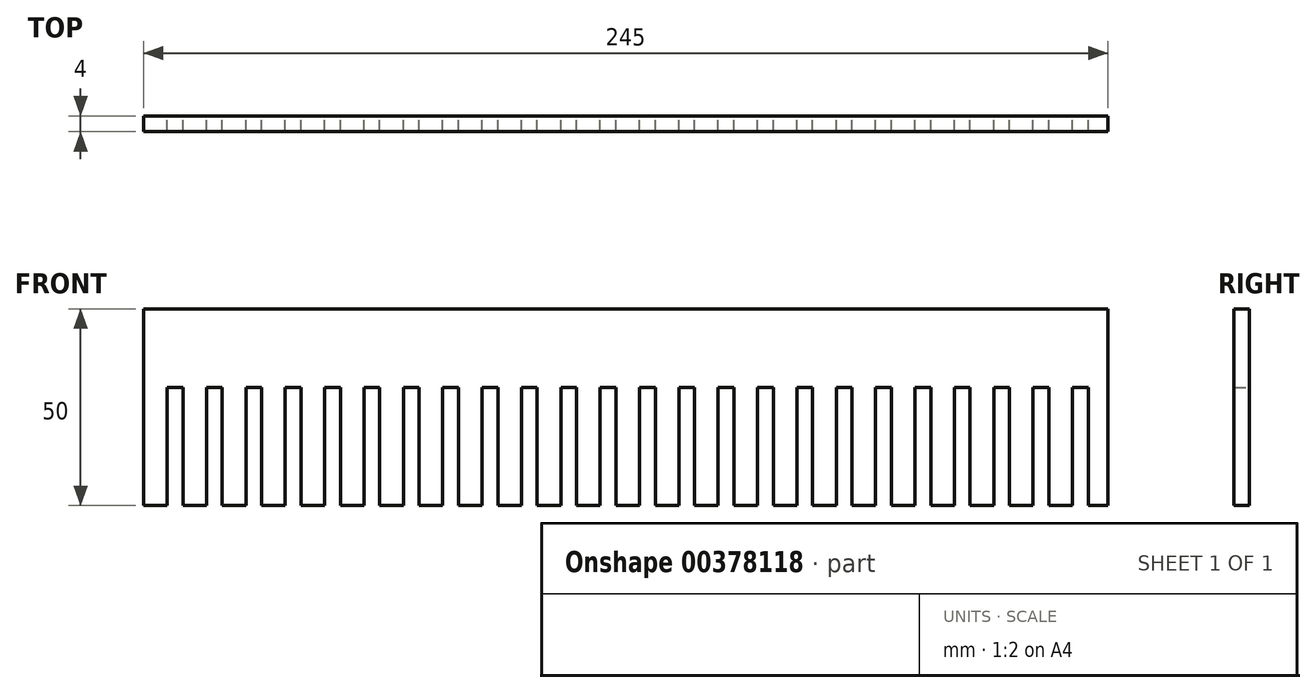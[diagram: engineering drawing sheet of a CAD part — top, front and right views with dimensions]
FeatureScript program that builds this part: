
annotation { "Feature Type Name" : "Feature", "Feature Type Description" : "" }
export const myFeature = defineFeature(function(context is Context, id is Id, definition is map)
    precondition{}
    {
        {
            var Q0;
            Q0=qCreatedBy(makeId("Front.planeOp"),FACE);
            var sketch = newSketch(context, id + "F0", { "sketchPlane" : qUnion([Q0])});
            skLineSegment(sketch, "E0", {"start": v(6, -20) * mm, "end": v(10, -20) * mm});
            skLineSegment(sketch, "E1", {"start": v(10, -20) * mm, "end": v(10, -50) * mm});
            skLineSegment(sketch, "E2.23.0.3", {"start": v(245, -50) * mm, "end": v(245, 0) * mm});
            skLineSegment(sketch, "E3", {"start": v(6, -20) * mm, "end": v(6, -50) * mm});
            skLineSegment(sketch, "E4", {"start": v(6, -50) * mm, "end": v(0, -50) * mm});
            skLineSegment(sketch, "E5", {"start": v(0, -50) * mm, "end": v(0, 0) * mm});
            skLineSegment(sketch, "E6", {"start": v(245, 0) * mm, "end": v(0, 0) * mm});
            skLineSegment(sketch, "E7.1.0.0", {"start": v(16, -50) * mm, "end": v(10, -50) * mm});
            skLineSegment(sketch, "E7.1.0.1", {"start": v(16, -20) * mm, "end": v(16, -50) * mm});
            skLineSegment(sketch, "E7.1.0.2", {"start": v(16, -20) * mm, "end": v(20, -20) * mm});
            skLineSegment(sketch, "E7.1.0.3", {"start": v(20, -20) * mm, "end": v(20, -50) * mm});
            skLineSegment(sketch, "E7.2.0.0", {"start": v(26, -50) * mm, "end": v(20, -50) * mm});
            skLineSegment(sketch, "E7.2.0.1", {"start": v(26, -20) * mm, "end": v(26, -50) * mm});
            skLineSegment(sketch, "E7.2.0.2", {"start": v(26, -20) * mm, "end": v(30, -20) * mm});
            skLineSegment(sketch, "E7.2.0.3", {"start": v(30, -20) * mm, "end": v(30, -50) * mm});
            skLineSegment(sketch, "E7.3.0.0", {"start": v(36, -50) * mm, "end": v(30, -50) * mm});
            skLineSegment(sketch, "E7.3.0.1", {"start": v(36, -20) * mm, "end": v(36, -50) * mm});
            skLineSegment(sketch, "E7.3.0.2", {"start": v(36, -20) * mm, "end": v(40, -20) * mm});
            skLineSegment(sketch, "E7.3.0.3", {"start": v(40, -20) * mm, "end": v(40, -50) * mm});
            skLineSegment(sketch, "E7.4.0.0", {"start": v(46, -50) * mm, "end": v(40, -50) * mm});
            skLineSegment(sketch, "E7.4.0.1", {"start": v(46, -20) * mm, "end": v(46, -50) * mm});
            skLineSegment(sketch, "E7.4.0.2", {"start": v(46, -20) * mm, "end": v(50, -20) * mm});
            skLineSegment(sketch, "E7.4.0.3", {"start": v(50, -20) * mm, "end": v(50, -50) * mm});
            skLineSegment(sketch, "E7.5.0.0", {"start": v(56, -50) * mm, "end": v(50, -50) * mm});
            skLineSegment(sketch, "E7.5.0.1", {"start": v(56, -20) * mm, "end": v(56, -50) * mm});
            skLineSegment(sketch, "E7.5.0.2", {"start": v(56, -20) * mm, "end": v(60, -20) * mm});
            skLineSegment(sketch, "E7.5.0.3", {"start": v(60, -20) * mm, "end": v(60, -50) * mm});
            skLineSegment(sketch, "E7.6.0.0", {"start": v(66, -50) * mm, "end": v(60, -50) * mm});
            skLineSegment(sketch, "E7.6.0.1", {"start": v(66, -20) * mm, "end": v(66, -50) * mm});
            skLineSegment(sketch, "E7.6.0.2", {"start": v(66, -20) * mm, "end": v(70, -20) * mm});
            skLineSegment(sketch, "E7.6.0.3", {"start": v(70, -20) * mm, "end": v(70, -50) * mm});
            skLineSegment(sketch, "E7.7.0.0", {"start": v(76, -50) * mm, "end": v(70, -50) * mm});
            skLineSegment(sketch, "E7.7.0.1", {"start": v(76, -20) * mm, "end": v(76, -50) * mm});
            skLineSegment(sketch, "E7.7.0.2", {"start": v(76, -20) * mm, "end": v(80, -20) * mm});
            skLineSegment(sketch, "E7.7.0.3", {"start": v(80, -20) * mm, "end": v(80, -50) * mm});
            skLineSegment(sketch, "E7.8.0.0", {"start": v(86, -50) * mm, "end": v(80, -50) * mm});
            skLineSegment(sketch, "E7.8.0.1", {"start": v(86, -20) * mm, "end": v(86, -50) * mm});
            skLineSegment(sketch, "E7.8.0.2", {"start": v(86, -20) * mm, "end": v(90, -20) * mm});
            skLineSegment(sketch, "E7.8.0.3", {"start": v(90, -20) * mm, "end": v(90, -50) * mm});
            skLineSegment(sketch, "E7.9.0.0", {"start": v(96, -50) * mm, "end": v(90, -50) * mm});
            skLineSegment(sketch, "E7.9.0.1", {"start": v(96, -20) * mm, "end": v(96, -50) * mm});
            skLineSegment(sketch, "E7.9.0.2", {"start": v(96, -20) * mm, "end": v(100, -20) * mm});
            skLineSegment(sketch, "E7.9.0.3", {"start": v(100, -20) * mm, "end": v(100, -50) * mm});
            skLineSegment(sketch, "E7.10.0.0", {"start": v(106, -50) * mm, "end": v(100, -50) * mm});
            skLineSegment(sketch, "E7.10.0.1", {"start": v(106, -20) * mm, "end": v(106, -50) * mm});
            skLineSegment(sketch, "E7.10.0.2", {"start": v(106, -20) * mm, "end": v(110, -20) * mm});
            skLineSegment(sketch, "E7.10.0.3", {"start": v(110, -20) * mm, "end": v(110, -50) * mm});
            skLineSegment(sketch, "E7.11.0.0", {"start": v(116, -50) * mm, "end": v(110, -50) * mm});
            skLineSegment(sketch, "E7.11.0.1", {"start": v(116, -20) * mm, "end": v(116, -50) * mm});
            skLineSegment(sketch, "E7.11.0.2", {"start": v(116, -20) * mm, "end": v(120, -20) * mm});
            skLineSegment(sketch, "E7.11.0.3", {"start": v(120, -20) * mm, "end": v(120, -50) * mm});
            skLineSegment(sketch, "E7.12.0.0", {"start": v(126, -50) * mm, "end": v(120, -50) * mm});
            skLineSegment(sketch, "E7.12.0.1", {"start": v(126, -20) * mm, "end": v(126, -50) * mm});
            skLineSegment(sketch, "E7.12.0.2", {"start": v(126, -20) * mm, "end": v(130, -20) * mm});
            skLineSegment(sketch, "E7.12.0.3", {"start": v(130, -20) * mm, "end": v(130, -50) * mm});
            skLineSegment(sketch, "E7.13.0.0", {"start": v(136, -50) * mm, "end": v(130, -50) * mm});
            skLineSegment(sketch, "E7.13.0.1", {"start": v(136, -20) * mm, "end": v(136, -50) * mm});
            skLineSegment(sketch, "E7.13.0.2", {"start": v(136, -20) * mm, "end": v(140, -20) * mm});
            skLineSegment(sketch, "E7.13.0.3", {"start": v(140, -20) * mm, "end": v(140, -50) * mm});
            skLineSegment(sketch, "E7.14.0.0", {"start": v(146, -50) * mm, "end": v(140, -50) * mm});
            skLineSegment(sketch, "E7.14.0.1", {"start": v(146, -20) * mm, "end": v(146, -50) * mm});
            skLineSegment(sketch, "E7.14.0.2", {"start": v(146, -20) * mm, "end": v(150, -20) * mm});
            skLineSegment(sketch, "E7.14.0.3", {"start": v(150, -20) * mm, "end": v(150, -50) * mm});
            skLineSegment(sketch, "E7.15.0.0", {"start": v(156, -50) * mm, "end": v(150, -50) * mm});
            skLineSegment(sketch, "E7.15.0.1", {"start": v(156, -20) * mm, "end": v(156, -50) * mm});
            skLineSegment(sketch, "E7.15.0.2", {"start": v(156, -20) * mm, "end": v(160, -20) * mm});
            skLineSegment(sketch, "E7.15.0.3", {"start": v(160, -20) * mm, "end": v(160, -50) * mm});
            skLineSegment(sketch, "E7.16.0.0", {"start": v(166, -50) * mm, "end": v(160, -50) * mm});
            skLineSegment(sketch, "E7.16.0.1", {"start": v(166, -20) * mm, "end": v(166, -50) * mm});
            skLineSegment(sketch, "E7.16.0.2", {"start": v(166, -20) * mm, "end": v(170, -20) * mm});
            skLineSegment(sketch, "E7.16.0.3", {"start": v(170, -20) * mm, "end": v(170, -50) * mm});
            skLineSegment(sketch, "E7.17.0.0", {"start": v(176, -50) * mm, "end": v(170, -50) * mm});
            skLineSegment(sketch, "E7.17.0.1", {"start": v(176, -20) * mm, "end": v(176, -50) * mm});
            skLineSegment(sketch, "E7.17.0.2", {"start": v(176, -20) * mm, "end": v(180, -20) * mm});
            skLineSegment(sketch, "E7.17.0.3", {"start": v(180, -20) * mm, "end": v(180, -50) * mm});
            skLineSegment(sketch, "E7.18.0.0", {"start": v(186, -50) * mm, "end": v(180, -50) * mm});
            skLineSegment(sketch, "E7.18.0.1", {"start": v(186, -20) * mm, "end": v(186, -50) * mm});
            skLineSegment(sketch, "E7.18.0.2", {"start": v(186, -20) * mm, "end": v(190, -20) * mm});
            skLineSegment(sketch, "E7.18.0.3", {"start": v(190, -20) * mm, "end": v(190, -50) * mm});
            skLineSegment(sketch, "E7.19.0.0", {"start": v(196, -50) * mm, "end": v(190, -50) * mm});
            skLineSegment(sketch, "E7.19.0.1", {"start": v(196, -20) * mm, "end": v(196, -50) * mm});
            skLineSegment(sketch, "E7.19.0.2", {"start": v(196, -20) * mm, "end": v(200, -20) * mm});
            skLineSegment(sketch, "E7.19.0.3", {"start": v(200, -20) * mm, "end": v(200, -50) * mm});
            skLineSegment(sketch, "E7.20.0.0", {"start": v(206, -50) * mm, "end": v(200, -50) * mm});
            skLineSegment(sketch, "E7.20.0.1", {"start": v(206, -20) * mm, "end": v(206, -50) * mm});
            skLineSegment(sketch, "E7.20.0.2", {"start": v(206, -20) * mm, "end": v(210, -20) * mm});
            skLineSegment(sketch, "E7.20.0.3", {"start": v(210, -20) * mm, "end": v(210, -50) * mm});
            skLineSegment(sketch, "E7.21.0.0", {"start": v(216, -50) * mm, "end": v(210, -50) * mm});
            skLineSegment(sketch, "E7.21.0.1", {"start": v(216, -20) * mm, "end": v(216, -50) * mm});
            skLineSegment(sketch, "E7.21.0.2", {"start": v(216, -20) * mm, "end": v(220, -20) * mm});
            skLineSegment(sketch, "E7.21.0.3", {"start": v(220, -20) * mm, "end": v(220, -50) * mm});
            skLineSegment(sketch, "E7.22.0.0", {"start": v(226, -50) * mm, "end": v(220, -50) * mm});
            skLineSegment(sketch, "E7.22.0.1", {"start": v(226, -20) * mm, "end": v(226, -50) * mm});
            skLineSegment(sketch, "E7.22.0.2", {"start": v(226, -20) * mm, "end": v(230, -20) * mm});
            skLineSegment(sketch, "E7.22.0.3", {"start": v(230, -20) * mm, "end": v(230, -50) * mm});
            skLineSegment(sketch, "E7.23.0.0", {"start": v(236, -50) * mm, "end": v(230, -50) * mm});
            skLineSegment(sketch, "E7.23.0.1", {"start": v(236, -20) * mm, "end": v(236, -50) * mm});
            skLineSegment(sketch, "E7.23.0.2", {"start": v(236, -20) * mm, "end": v(240, -20) * mm});
            skLineSegment(sketch, "E7.23.0.3", {"start": v(240, -20) * mm, "end": v(240, -50) * mm});
            skLineSegment(sketch, "E7.direction1", {"start": v(0, -50) * mm, "end": v(10, -50) * mm, "construction": true});
            skLineSegment(sketch, "E8", {"start": v(240, -50) * mm, "end": v(245, -50) * mm});
            skSolve(sketch);
        }
        {
            var Q0;
            Q0=makeQuery(id+"F0.imprint","IMPRINT",FACE,{"disambiguationData":[TD([[makeQuery(id+"F0.imprint","IMPRINT",EDGE,{"derivedFrom":sQuery(id+"F0.wireOp",EDGE,"E0")}),1.0]])]});
            extrude(context, id + "F1", {"entities" : qUnion([Q0]), "depth" : 4 * mm});
        }
    });
